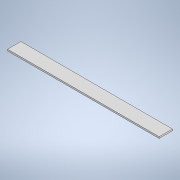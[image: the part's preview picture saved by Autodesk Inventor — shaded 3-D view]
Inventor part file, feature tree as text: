
AUTODESK INVENTOR PART (.ipt)
format: ipt  version: 2020 (Build 240168000, 168)  size: 92,672 bytes
history: native  units: mm
features: extrude x1, sketch x1
ambient origin geometry x8: Origin, YZ Plane, XZ Plane, XY Plane, X Axis, Y Axis, Z Axis, Center Point
bodies: Solid1 (feature_tree)
feature tree (2):
  extrude  "Extrusion1"  Depth=285.0mm
  sketch  "Sketch1"  dims[d0=25.0mm d1=285.0mm d2=3.0mm d3=0.0mm]
